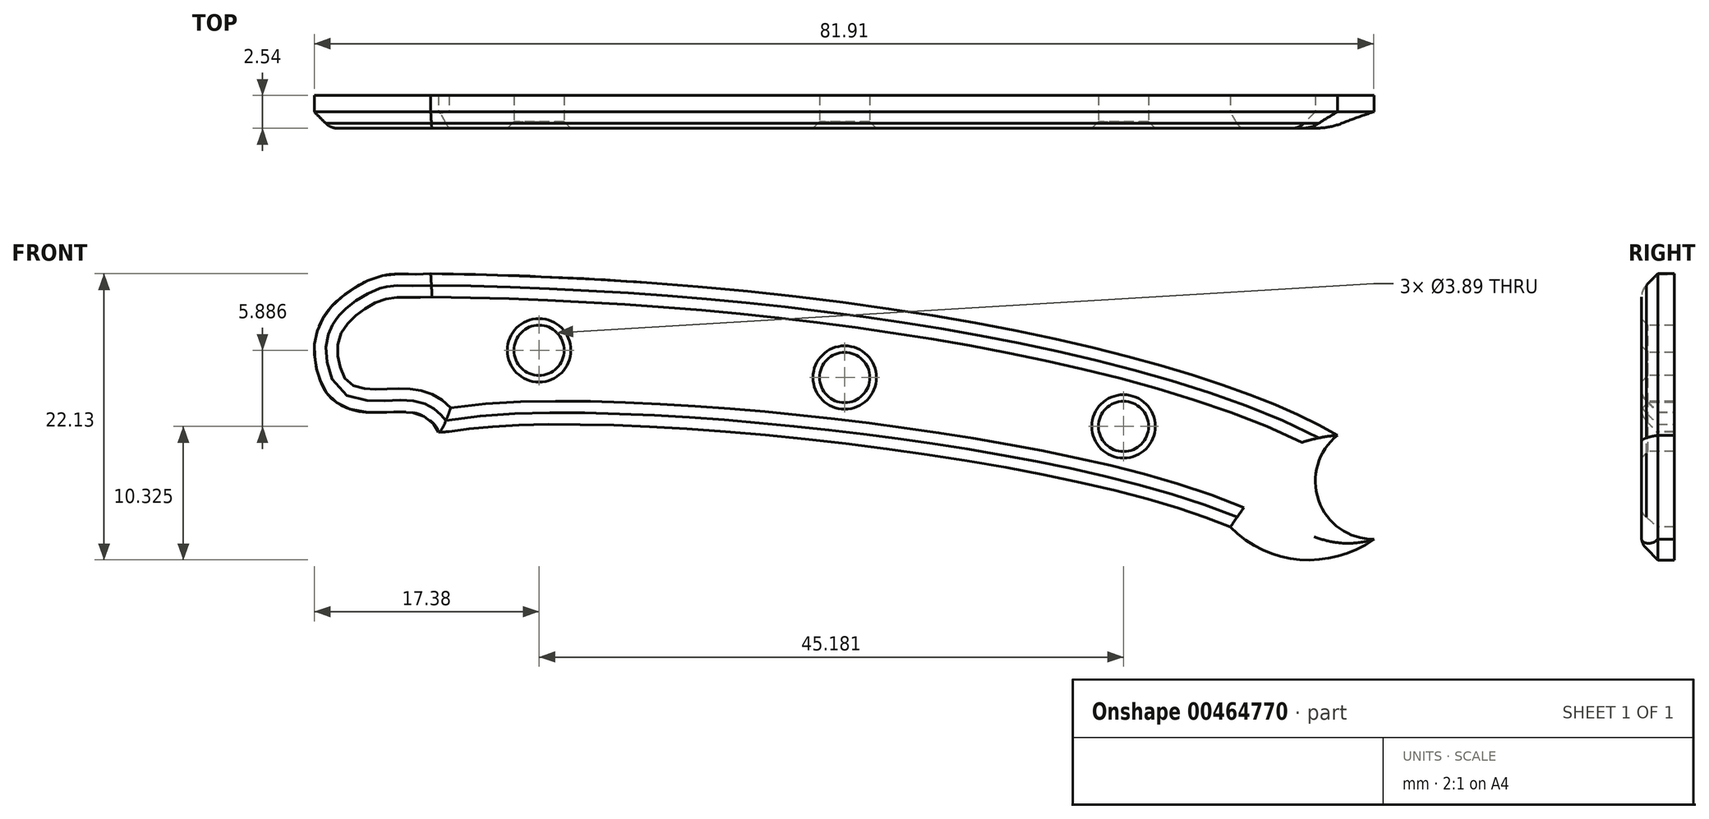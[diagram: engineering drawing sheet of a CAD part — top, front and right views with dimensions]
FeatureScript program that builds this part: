
annotation { "Feature Type Name" : "Feature", "Feature Type Description" : "" }
export const myFeature = defineFeature(function(context is Context, id is Id, definition is map)
    precondition{}
    {
        {
            var Q0;
            Q0=qCreatedBy(makeId("Front.planeOp"),FACE);
            var sketch = newSketch(context, id + "F0", { "sketchPlane" : qUnion([Q0])});
            skPoint(sketch, "E0", {"position": v(37.7, 34.47) * mm});
            skFitSpline(sketch, "E1", {"points": [v(7.11, 24.48) * mm, v(67.5, 17.12) * mm], "startDerivative": vector(32.5, 6.07) * mm, "endDerivative": vector(41.2, -17.48) * mm});
            skPoint(sketch, "E2", {"position": v(37.7, 23.57) * mm});
            skArc(sketch, "E3", {"start": v(67.5, 17.12) * mm, "mid": v(73.61, 14.57) * mm, "end": v(79.71, 17.12) * mm});
            skCircle(sketch, "E4", {"center": v(76.86, 19.24) * mm, "radius": 1.72 * mm});
            skCircle(sketch, "E5", {"center": v(14.07, 30.78) * mm, "radius": 1.94 * mm});
            skCircle(sketch, "E6", {"center": v(37.7, 28.68) * mm, "radius": 1.94 * mm});
            skCircle(sketch, "E7", {"center": v(59.25, 24.9) * mm, "radius": 1.94 * mm});
            skPoint(sketch, "E8", {"position": v(14.07, 36.48) * mm});
            skPoint(sketch, "E9", {"position": v(41.42, 33.95) * mm});
            skPoint(sketch, "E10", {"position": v(59.25, 30.4) * mm});
            skFitSpline(sketch, "E11", {"points": [v(5.7, 36.7) * mm, v(2.38, 36.62) * mm, v(-0.4, 35.48) * mm, v(-2.43, 33.6) * mm, v(-3.28, 31.36) * mm, v(-3.14, 29.43) * mm, v(-2.3, 27.4) * mm, v(0, 26.08) * mm, v(3.52, 26.03) * mm, v(5.36, 25.57) * mm, v(6.3, 24.46) * mm], "startDerivative": vector(-24.15, -3.51) * mm, "endDerivative": vector(1.15, -12.96) * mm});
            skFitSpline(sketch, "E12.trimOffspring", {"points": [v(-69.47, 27.87) * mm, v(79.71, 17.12) * mm], "startDerivative": vector(238.36, 61.55) * mm, "endDerivative": vector(-26.8, -33.68) * mm});
            skCircle(sketch, "E13", {"center": v(78.58, 20.67) * mm, "radius": 4.5 * mm});
            skLineSegment(sketch, "E14", {"start": v(7.11, 24.48) * mm, "end": v(6.3, 24.46) * mm});
            skSolve(sketch);
        }
        {
            var Q0;
            {var subQ1=sQuery(id+"F0.wireOp",EDGE,"E1");Q0=makeQuery(id+"F0.imprint","IMPRINT",FACE,{"disambiguationData":[TD([[makeQuery(id+"F0.imprint","IMPRINT",EDGE,{"derivedFrom":subQ1}),1.0]])]});}
            extrude(context, id + "F1", {"entities" : qUnion([Q0]), "oppositeDirection" : true, "depth" : 2.54 * mm});
        }
        {
            var Q0;
            Q0=makeQuery(id+"F1.opExtrude","CAP_EDGE",EDGE,{"disambiguationData":[OSD([sQuery(id+"F0.wireOp",EDGE,"E12.trimOffspring")])],"isStart":true});
            var Q1;
            Q1=makeQuery(id+"F1.opExtrude","CAP_EDGE",EDGE,{"disambiguationData":[OSD([sQuery(id+"F0.wireOp",EDGE,"E1")])],"isStart":true});
            var Q2;
            Q2=makeQuery(id+"F1.opExtrude","CAP_EDGE",EDGE,{"disambiguationData":[OSD([sQuery(id+"F0.wireOp",EDGE,"E3")])],"isStart":true});
            var Q3;
            Q3=makeQuery(id+"F1.opExtrude","CAP_EDGE",EDGE,{"disambiguationData":[OSD([sQuery(id+"F0.wireOp",EDGE,"E13")])],"isStart":true});
            var Q4;
            Q4=makeQuery(id+"F1.opExtrude","CAP_EDGE",EDGE,{"disambiguationData":[OSD([sQuery(id+"F0.wireOp",EDGE,"E11")])],"isStart":true});
            var Q5;
            Q5=makeQuery(id+"F1.opExtrude","CAP_EDGE",EDGE,{"disambiguationData":[OSD([sQuery(id+"F0.wireOp",EDGE,"E14")])],"isStart":true});
            chamfer(context, id + "F2", {"entities" : qUnion([Q0, Q1, Q2, Q3, Q4, Q5]), "width" : 1.27 * mm, "tangentPropagation" : true});
        }
        {
            var Q0;
            {var subQ0=sQuery(id+"F0.wireOp",EDGE,"E12.trimOffspring");Q0=makeQuery(id+"F2.opChamfer","BLEND_EDGE",EDGE,{"blendedFrom":[makeQuery(id+"F1.opExtrude","CAP_EDGE",EDGE,{"disambiguationData":[OSD([subQ0])],"isStart":true}),makeQuery(id+"F1.opExtrude","CAP_FACE",FACE,{"disambiguationData":[OSD([sQuery(id+"F0.wireOp",EDGE,"E1"),sQuery(id+"F0.wireOp",EDGE,"E3"),sQuery(id+"F0.wireOp",EDGE,"E5"),sQuery(id+"F0.wireOp",EDGE,"E6"),sQuery(id+"F0.wireOp",EDGE,"E7"),sQuery(id+"F0.wireOp",EDGE,"E11"),subQ0,sQuery(id+"F0.wireOp",EDGE,"E13"),sQuery(id+"F0.wireOp",EDGE,"E14")])],"isStart":true})],"blendedInto":[makeQuery(id+"F1.opExtrude","CAP_FACE",FACE,{"disambiguationData":[OSD([sQuery(id+"F0.wireOp",EDGE,"E1"),sQuery(id+"F0.wireOp",EDGE,"E3"),sQuery(id+"F0.wireOp",EDGE,"E5"),sQuery(id+"F0.wireOp",EDGE,"E6"),sQuery(id+"F0.wireOp",EDGE,"E7"),sQuery(id+"F0.wireOp",EDGE,"E11"),subQ0,sQuery(id+"F0.wireOp",EDGE,"E13"),sQuery(id+"F0.wireOp",EDGE,"E14")])],"isStart":true})]});}
            var Q1;
            {var subQ0=sQuery(id+"F0.wireOp",EDGE,"E1");Q1=makeQuery(id+"F2.opChamfer","BLEND_EDGE",EDGE,{"blendedFrom":[makeQuery(id+"F1.opExtrude","CAP_EDGE",EDGE,{"disambiguationData":[OSD([subQ0])],"isStart":true}),makeQuery(id+"F1.opExtrude","CAP_FACE",FACE,{"disambiguationData":[OSD([subQ0,sQuery(id+"F0.wireOp",EDGE,"E3"),sQuery(id+"F0.wireOp",EDGE,"E5"),sQuery(id+"F0.wireOp",EDGE,"E6"),sQuery(id+"F0.wireOp",EDGE,"E7"),sQuery(id+"F0.wireOp",EDGE,"E11"),sQuery(id+"F0.wireOp",EDGE,"E12.trimOffspring"),sQuery(id+"F0.wireOp",EDGE,"E13"),sQuery(id+"F0.wireOp",EDGE,"E14")])],"isStart":true})],"blendedInto":[makeQuery(id+"F1.opExtrude","CAP_FACE",FACE,{"disambiguationData":[OSD([subQ0,sQuery(id+"F0.wireOp",EDGE,"E3"),sQuery(id+"F0.wireOp",EDGE,"E5"),sQuery(id+"F0.wireOp",EDGE,"E6"),sQuery(id+"F0.wireOp",EDGE,"E7"),sQuery(id+"F0.wireOp",EDGE,"E11"),sQuery(id+"F0.wireOp",EDGE,"E12.trimOffspring"),sQuery(id+"F0.wireOp",EDGE,"E13"),sQuery(id+"F0.wireOp",EDGE,"E14")])],"isStart":true})]});}
            var Q2;
            {var subQ0=sQuery(id+"F0.wireOp",EDGE,"E13");Q2=makeQuery(id+"F2.opChamfer","BLEND_EDGE",EDGE,{"blendedFrom":[makeQuery(id+"F1.opExtrude","CAP_EDGE",EDGE,{"disambiguationData":[OSD([subQ0])],"isStart":true}),makeQuery(id+"F1.opExtrude","CAP_FACE",FACE,{"disambiguationData":[OSD([sQuery(id+"F0.wireOp",EDGE,"E1"),sQuery(id+"F0.wireOp",EDGE,"E3"),sQuery(id+"F0.wireOp",EDGE,"E5"),sQuery(id+"F0.wireOp",EDGE,"E6"),sQuery(id+"F0.wireOp",EDGE,"E7"),sQuery(id+"F0.wireOp",EDGE,"E11"),sQuery(id+"F0.wireOp",EDGE,"E12.trimOffspring"),subQ0,sQuery(id+"F0.wireOp",EDGE,"E14")])],"isStart":true})],"blendedInto":[makeQuery(id+"F1.opExtrude","CAP_FACE",FACE,{"disambiguationData":[OSD([sQuery(id+"F0.wireOp",EDGE,"E1"),sQuery(id+"F0.wireOp",EDGE,"E3"),sQuery(id+"F0.wireOp",EDGE,"E5"),sQuery(id+"F0.wireOp",EDGE,"E6"),sQuery(id+"F0.wireOp",EDGE,"E7"),sQuery(id+"F0.wireOp",EDGE,"E11"),sQuery(id+"F0.wireOp",EDGE,"E12.trimOffspring"),subQ0,sQuery(id+"F0.wireOp",EDGE,"E14")])],"isStart":true})]});}
            var Q3;
            {var subQ0=sQuery(id+"F0.wireOp",EDGE,"E11");Q3=makeQuery(id+"F2.opChamfer","BLEND_EDGE",EDGE,{"blendedFrom":[makeQuery(id+"F1.opExtrude","CAP_EDGE",EDGE,{"disambiguationData":[OSD([subQ0])],"isStart":true}),makeQuery(id+"F1.opExtrude","CAP_FACE",FACE,{"disambiguationData":[OSD([sQuery(id+"F0.wireOp",EDGE,"E1"),sQuery(id+"F0.wireOp",EDGE,"E3"),sQuery(id+"F0.wireOp",EDGE,"E5"),sQuery(id+"F0.wireOp",EDGE,"E6"),sQuery(id+"F0.wireOp",EDGE,"E7"),subQ0,sQuery(id+"F0.wireOp",EDGE,"E12.trimOffspring"),sQuery(id+"F0.wireOp",EDGE,"E13"),sQuery(id+"F0.wireOp",EDGE,"E14")])],"isStart":true})],"blendedInto":[makeQuery(id+"F1.opExtrude","CAP_FACE",FACE,{"disambiguationData":[OSD([sQuery(id+"F0.wireOp",EDGE,"E1"),sQuery(id+"F0.wireOp",EDGE,"E3"),sQuery(id+"F0.wireOp",EDGE,"E5"),sQuery(id+"F0.wireOp",EDGE,"E6"),sQuery(id+"F0.wireOp",EDGE,"E7"),subQ0,sQuery(id+"F0.wireOp",EDGE,"E12.trimOffspring"),sQuery(id+"F0.wireOp",EDGE,"E13"),sQuery(id+"F0.wireOp",EDGE,"E14")])],"isStart":true})]});}
            var Q4;
            {var subQ0=sQuery(id+"F0.wireOp",EDGE,"E3");Q4=makeQuery(id+"F2.opChamfer","BLEND_EDGE",EDGE,{"blendedFrom":[makeQuery(id+"F1.opExtrude","CAP_EDGE",EDGE,{"disambiguationData":[OSD([subQ0])],"isStart":true}),makeQuery(id+"F1.opExtrude","CAP_FACE",FACE,{"disambiguationData":[OSD([sQuery(id+"F0.wireOp",EDGE,"E1"),subQ0,sQuery(id+"F0.wireOp",EDGE,"E5"),sQuery(id+"F0.wireOp",EDGE,"E6"),sQuery(id+"F0.wireOp",EDGE,"E7"),sQuery(id+"F0.wireOp",EDGE,"E11"),sQuery(id+"F0.wireOp",EDGE,"E12.trimOffspring"),sQuery(id+"F0.wireOp",EDGE,"E13"),sQuery(id+"F0.wireOp",EDGE,"E14")])],"isStart":true})],"blendedInto":[makeQuery(id+"F1.opExtrude","CAP_FACE",FACE,{"disambiguationData":[OSD([sQuery(id+"F0.wireOp",EDGE,"E1"),subQ0,sQuery(id+"F0.wireOp",EDGE,"E5"),sQuery(id+"F0.wireOp",EDGE,"E6"),sQuery(id+"F0.wireOp",EDGE,"E7"),sQuery(id+"F0.wireOp",EDGE,"E11"),sQuery(id+"F0.wireOp",EDGE,"E12.trimOffspring"),sQuery(id+"F0.wireOp",EDGE,"E13"),sQuery(id+"F0.wireOp",EDGE,"E14")])],"isStart":true})]});}
            fillet(context, id + "F3", {"entities" : qUnion([Q0, Q1, Q2, Q3, Q4]), "radius" : 1.27 * mm, "allowEdgeOverflow" : false});
        }
        {
            var Q0;
            Q0=makeQuery(id+"F1.opExtrude","CAP_EDGE",EDGE,{"disambiguationData":[OSD([sQuery(id+"F0.wireOp",EDGE,"E5")])],"isStart":true});
            var Q1;
            Q1=makeQuery(id+"F1.opExtrude","CAP_EDGE",EDGE,{"disambiguationData":[OSD([sQuery(id+"F0.wireOp",EDGE,"E6")])],"isStart":true});
            var Q2;
            Q2=makeQuery(id+"F1.opExtrude","CAP_EDGE",EDGE,{"disambiguationData":[OSD([sQuery(id+"F0.wireOp",EDGE,"E7")])],"isStart":true});
            chamfer(context, id + "F4", {"entities" : qUnion([Q0, Q1, Q2]), "width" : 0.5 * mm, "tangentPropagation" : true});
        }
    });
